# Revit family: ADB Fourneaux Gaz L7002
name_source: partatom
category: Equipement spécialisé
units: mm (PartAtom-declared; Revit-internal decimal feet)

## family parameters
Basée sur le plan de construction = Non
Conserver l'orientation des annotations = Non
Cote de connecteur circulaire = Utiliser le diamètre
Couper avec des vides une fois chargée = Non
Numéro OmniClass = 23.40.40.14.17.11
Partagée = Non
Repère de localisation dans la pièce = Non
Titre OmniClass = Cookers, Ovens, Stoves
Toujours verticalement = Oui
Type d'élément = Normal

## types (4) — shared parameters
Commentaires du type = Gamme Ambassade - Fourneaux gaz
Diamètre de Raccordement Gaz = 21 mm
Fabricant = Société Industrielle de Lacanche
Pbase = 0 W
URL = https://www.ambassade-de-bourgogne.com
zero-valued in all types: Elévation par défaut

## per-type parameters (varying)
| type | Bouton hors CG 721 GAGCF | Description | Modèle | Pbase gaz | Plaques | Poids net à vide |
| 1 plaque coup de feu 650 X 500- 1 four - CG 721 GAGCF | Non | Fourneau avec plaque coup de feu 650 X 500 - 1 four gaz Gastronome 1/1 | CG 721 GAGCF | 10 W | CG731_CG741_CG731CF_CG721GACF_Fourneaux 4-3-2 feux vifs : CG 721 GAGCF | 95.00 kg |
| 4 feux vifs - 1 four - CG 741 | Oui | Fourneau 4 feux vifs - 1 four gaz Gastronome 1/1 | CG 741 | 17 W | CG731_CG741_CG731CF_CG721GACF_Fourneaux 4-3-2 feux vifs : CG 741 | 91.00 kg |
| 2 feux vifs - 1 plaque coup de feu - 1 four - CG 731 CF | Oui | Fourneau 2 feux vifs - 1 plaque coup de feu - 1 four gaz Gastronome 1/1 | CG 731 CF | 17 W | CG731_CG741_CG731CF_CG721GACF_Fourneaux 4-3-2 feux vifs : CG 731 CF | 96.00 kg |
| 3 feux vifs - 1 four - CG 731 | Oui | Fourneau 3 feux vifs - 1 four gaz Gastronome 1/1 | CG 731 | 17 W | CG731_CG741_CG731CF_CG721GACF_Fourneaux 4-3-2 feux vifs : CG 731 | 85.00 kg |
